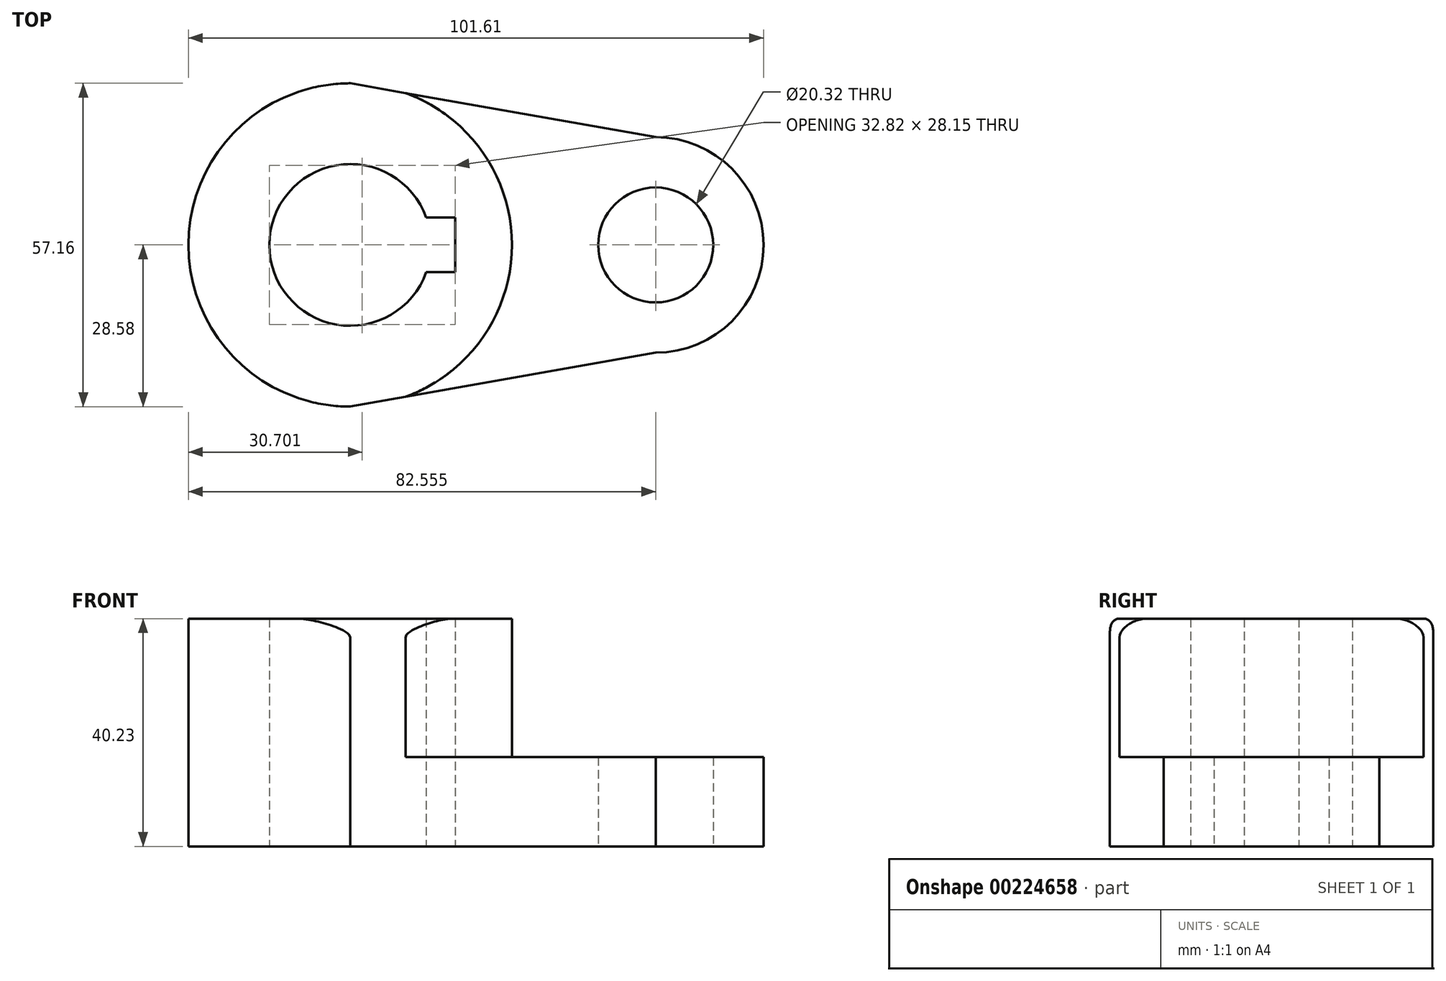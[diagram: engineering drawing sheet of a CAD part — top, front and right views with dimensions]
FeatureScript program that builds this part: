
annotation { "Feature Type Name" : "Feature", "Feature Type Description" : "" }
export const myFeature = defineFeature(function(context is Context, id is Id, definition is map)
    precondition{}
    {
        {
            var Q0;
            Q0=qCreatedBy(makeId("Top.planeOp"),FACE);
            var sketch = newSketch(context, id + "F0", { "sketchPlane" : qUnion([Q0])});
            skCircle(sketch, "E0", {"center": v(0, 0) * mm, "radius": 28.58 * mm});
            skCircle(sketch, "E1", {"center": v(0, 0) * mm, "radius": 14.29 * mm});
            skCircle(sketch, "E2", {"center": v(53.98, 0) * mm, "radius": 10.16 * mm});
            skLineSegment(sketch, "E3.bottom", {"start": v(18.53, 4.83) * mm, "end": v(-18.53, 4.83) * mm});
            skLineSegment(sketch, "E3.top", {"start": v(18.53, -4.83) * mm, "end": v(-18.53, -4.83) * mm});
            skLineSegment(sketch, "E3.left", {"start": v(18.53, 4.83) * mm, "end": v(18.53, -4.83) * mm});
            skLineSegment(sketch, "E3.right", {"start": v(-18.53, 4.83) * mm, "end": v(-18.53, -4.83) * mm});
            skLineSegment(sketch, "E4", {"start": v(0, 0) * mm, "end": v(0, 28.57) * mm});
            skPoint(sketch, "E4.startSnap0", {"position": v(0, 4.83) * mm});
            skLineSegment(sketch, "E5", {"start": v(0, -28.57) * mm, "end": v(53.98, -19.05) * mm});
            skLineSegment(sketch, "E6", {"start": v(0, 28.57) * mm, "end": v(53.98, 19.05) * mm});
            skArc(sketch, "E7", {"start": v(53.98, -19.05) * mm, "mid": v(73.03, 0) * mm, "end": v(53.98, 19.05) * mm});
            skSolve(sketch);
        }
        {
            var Q0;
            Q0=makeQuery(id+"F0.imprint","IMPRINT",FACE,{"disambiguationData":[TD([[makeQuery(id+"F0.imprint","IMPRINT",EDGE,{"derivedFrom":sQuery(id+"F0.wireOp",EDGE,"E2")}),-1.0]])]});
            extrude(context, id + "F1", {"entities" : qUnion([Q0]), "depth" : 15.77 * mm});
        }
        {
            var Q0;
            {var subQ0=sQuery(id+"F0.wireOp",EDGE,"E3.left");Q0=makeQuery(id+"F0.imprint","IMPRINT",FACE,{"disambiguationData":[TD([[makeQuery(id+"F0.imprint","IMPRINT",EDGE,{"derivedFrom":subQ0}),1.0]])]});}
            var Q1;
            {var subQ5=sQuery(id+"F0.wireOp",EDGE,"E3.right");Q1=makeQuery(id+"F0.imprint","IMPRINT",FACE,{"disambiguationData":[TD([[makeQuery(id+"F0.imprint","IMPRINT",EDGE,{"derivedFrom":subQ5}),1.0]])]});}
            extrude(context, id + "F2", {"entities" : qUnion([Q0, Q1]), "operationType" : NewBodyOperationType.ADD, "depth" : 40.23 * mm});
        }
        {
            var Q0;
            {var subQ0=sQuery(id+"F0.wireOp",EDGE,"E0");Q0=makeQuery(id+"F2.opExtrude","CAP_EDGE",EDGE,{"disambiguationData":[OSD([subQ0]),TDD([makeQuery(id+"F0.imprint","IMPRINT",EDGE,{"disambiguationData":[TD([[makeQuery(id+"F0.imprint","INTERSECT",VERTEX,{"disambiguationData":[OD(1.0)],"derivedFrom":[subQ0,sQuery(id+"F0.wireOp",EDGE,"E6")]}),1.0]])],"derivedFrom":subQ0})])],"isStart":false});}
            var Q1;
            {var subQ0=sQuery(id+"F0.wireOp",EDGE,"E0");Q1=makeQuery(id+"F2.opExtrude","CAP_EDGE",EDGE,{"disambiguationData":[OSD([subQ0]),TDD([makeQuery(id+"F0.imprint","IMPRINT",EDGE,{"disambiguationData":[TD([[makeQuery(id+"F0.imprint","INTERSECT",VERTEX,{"disambiguationData":[OD(0.0)],"derivedFrom":[subQ0,sQuery(id+"F0.wireOp",EDGE,"E6")]}),-1.0]])],"derivedFrom":subQ0})])],"isStart":false});}
            var Q2;
            Q2=makeQuery(id+"F2.opExtrude","CAP_EDGE",EDGE,{"disambiguationData":[OSD([sQuery(id+"F0.wireOp",EDGE,"E6")])],"isStart":false});
            var Q3;
            Q3=makeQuery(id+"F2.opExtrude","CAP_EDGE",EDGE,{"disambiguationData":[OSD([sQuery(id+"F0.wireOp",EDGE,"E5")])],"isStart":false});
            fillet(context, id + "F3", {"entities" : qUnion([Q0, Q1, Q2, Q3]), "radius" : 3.3 * mm, "tangentPropagation" : true, "allowEdgeOverflow" : false});
        }
    });
